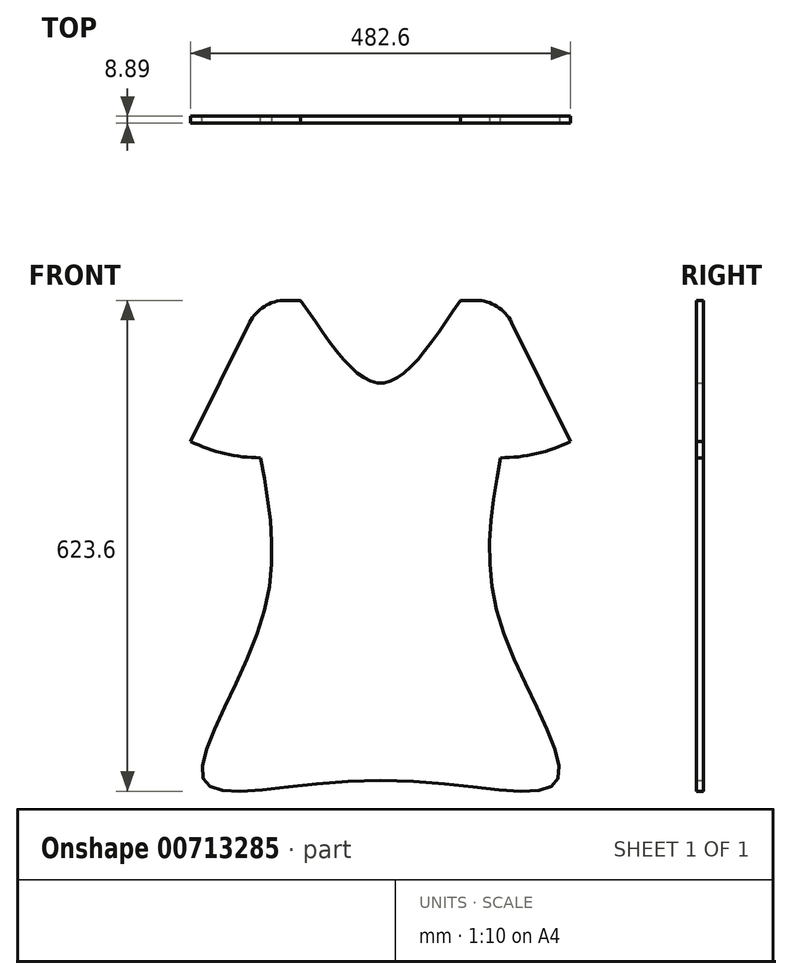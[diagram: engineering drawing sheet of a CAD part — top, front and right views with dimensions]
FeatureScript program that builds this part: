
annotation { "Feature Type Name" : "Feature", "Feature Type Description" : "" }
export const myFeature = defineFeature(function(context is Context, id is Id, definition is map)
    precondition{}
    {
        {
            var Q0;
            Q0=qCreatedBy(makeId("Front.planeOp"),FACE);
            var sketch = newSketch(context, id + "F0", { "sketchPlane" : qUnion([Q0])});
            skLineSegment(sketch, "E0.bottom", {"start": v(-241.3, 0) * mm, "end": v(241.3, 0) * mm, "construction": true});
            skLineSegment(sketch, "E0.top", {"start": v(-241.3, -609.6) * mm, "end": v(241.3, -609.6) * mm, "construction": true});
            skLineSegment(sketch, "E0.left", {"start": v(-241.3, 0) * mm, "end": v(-241.3, -609.6) * mm, "construction": true});
            skLineSegment(sketch, "E0.right", {"start": v(241.3, 0) * mm, "end": v(241.3, -609.6) * mm, "construction": true});
            skLineSegment(sketch, "E1", {"start": v(0, 249.25) * mm, "end": v(0, -609.6) * mm, "construction": true});
            skLineSegment(sketch, "E2", {"start": v(-166.4, -28.22) * mm, "end": v(-241.3, -179.16) * mm});
            skArc(sketch, "E3", {"start": v(-241.3, -179.16) * mm, "mid": v(-198.06, -194.72) * mm, "end": v(-152.4, -200) * mm});
            skLineSegment(sketch, "E4", {"start": v(-120.9, 0) * mm, "end": v(-101.6, 0) * mm});
            skArc(sketch, "E5.MirrorCS", {"start": v(241.3, -179.16) * mm, "mid": v(198.06, -194.72) * mm, "end": v(152.4, -200) * mm});
            skLineSegment(sketch, "E6.MirrorCS", {"start": v(166.4, -28.22) * mm, "end": v(241.3, -179.16) * mm});
            skLineSegment(sketch, "E7.MirrorCS", {"start": v(120.9, 0) * mm, "end": v(101.6, 0) * mm});
            skFitSpline(sketch, "E8", {"points": [v(101.6, 0) * mm, v(0, -105.2) * mm, v(-101.6, 0) * mm], "startDerivative": vector(-218.4, -315.6) * mm, "endDerivative": vector(-218.4, 315.6) * mm});
            skArc(sketch, "E9.filletArc", {"start": v(166.4, -28.22) * mm, "mid": v(147.67, -7.63) * mm, "end": v(120.9, 0) * mm});
            skArc(sketch, "E10.filletArc", {"start": v(-120.9, 0) * mm, "mid": v(-147.67, -7.63) * mm, "end": v(-166.4, -28.22) * mm});
            skFitSpline(sketch, "E11", {"points": [v(152.4, -200) * mm, v(152.4, -411.32) * mm, v(224.5, -609.6) * mm, v(0, -609.6) * mm], "startDerivative": vector(-108.5, -608.91) * mm, "endDerivative": vector(-969.87, 0) * mm});
            skFitSpline(sketch, "E12.MirrorCS", {"points": [v(-152.4, -200) * mm, v(-152.4, -411.32) * mm, v(-224.5, -609.6) * mm, v(0, -609.6) * mm], "startDerivative": vector(108.5, -608.91) * mm, "endDerivative": vector(969.87, 0) * mm});
            skSolve(sketch);
        }
        {
            var Q0;
            Q0=qSketchRegion(id+"F0",true);
            extrude(context, id + "F1", {"entities" : qUnion([Q0]), "depth" : 8.9 * mm, "offsetDistance" : 25.4 * mm});
        }
    });
